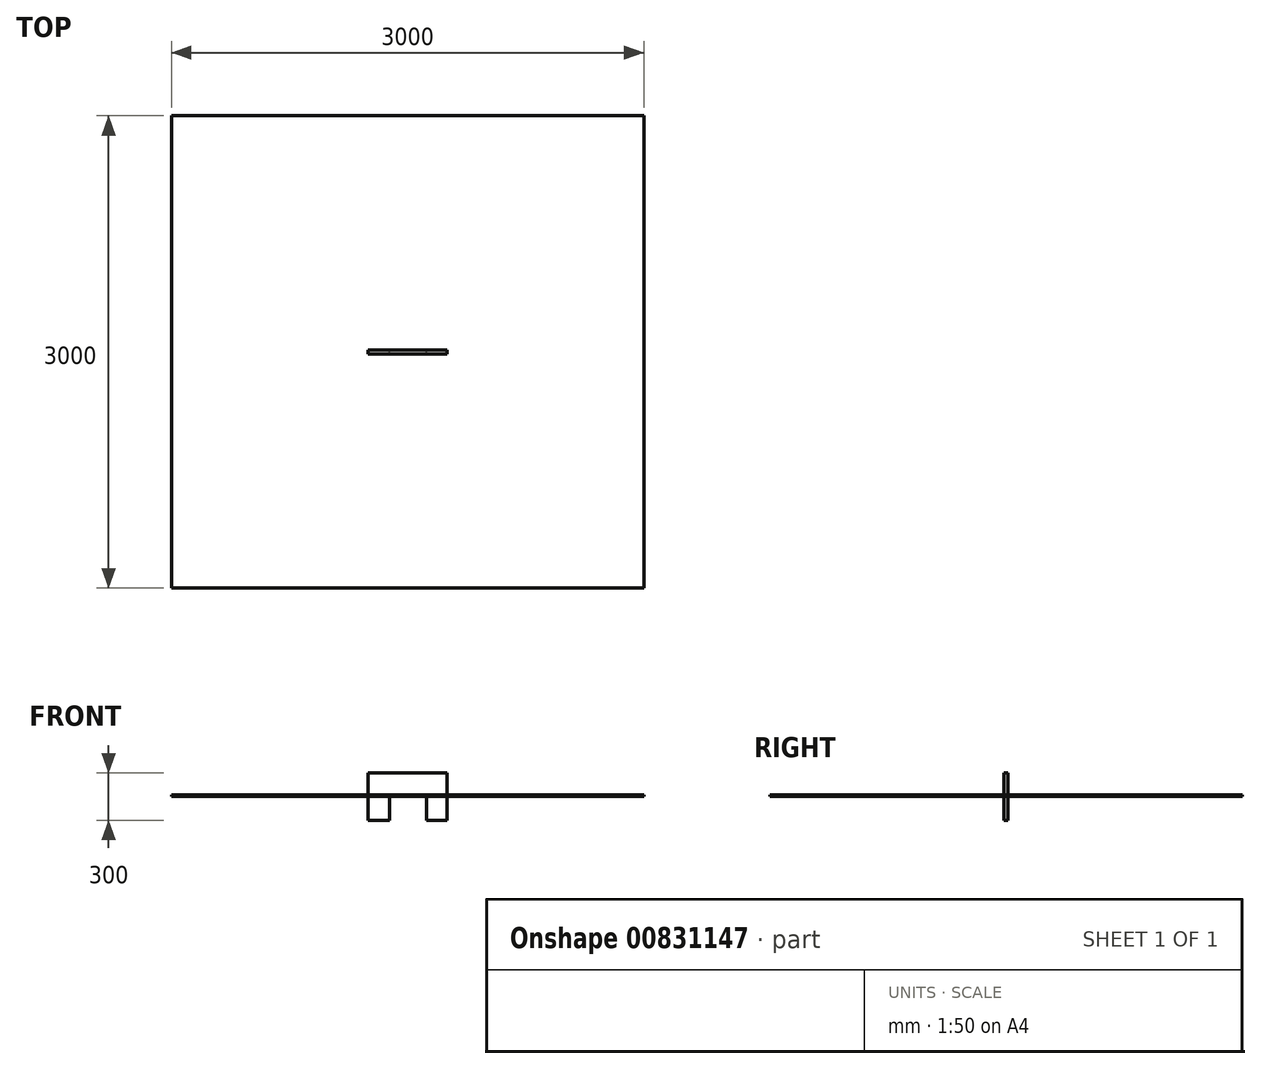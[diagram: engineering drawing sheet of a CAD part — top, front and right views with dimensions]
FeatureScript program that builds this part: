
annotation { "Feature Type Name" : "Feature", "Feature Type Description" : "" }
export const myFeature = defineFeature(function(context is Context, id is Id, definition is map)
    precondition{}
    {
        {
            var Q0;
            Q0=qCreatedBy(makeId("Top.planeOp"),FACE);
            var sketch = newSketch(context, id + "F0", { "sketchPlane" : qUnion([Q0])});
            skLineSegment(sketch, "E0.bottom", {"start": v(-1500, -1500) * mm, "end": v(1500, -1500) * mm});
            skLineSegment(sketch, "E0.top", {"start": v(-1500, 1500) * mm, "end": v(1500, 1500) * mm});
            skLineSegment(sketch, "E0.left", {"start": v(-1500, -1500) * mm, "end": v(-1500, 1500) * mm});
            skLineSegment(sketch, "E0.right", {"start": v(1500, -1500) * mm, "end": v(1500, 1500) * mm});
            skSolve(sketch);
        }
        {
            var Q0;
            Q0 = qSketchRegion(id + "F0", true);
            extrude(context, id + "F1", {"entities" : qUnion([Q0]), "depth" : 10 * mm, "offsetDistance" : 25 * mm});
        }
        {
            var Q0;
            Q0=qCreatedBy(makeId("Front.planeOp"),FACE);
            var sketch = newSketch(context, id + "F2", { "sketchPlane" : qUnion([Q0])});
            skLineSegment(sketch, "E1.bottom", {"start": v(-250, 150) * mm, "end": v(250, 150) * mm});
            skLineSegment(sketch, "E1.top", {"start": v(-250, -150) * mm, "end": v(-114.3, -150) * mm});
            skLineSegment(sketch, "E1.left", {"start": v(-250, 150) * mm, "end": v(-250, -150) * mm});
            skLineSegment(sketch, "E1.right", {"start": v(250, 150) * mm, "end": v(250, -150) * mm});
            skLineSegment(sketch, "E2.top", {"start": v(-114.3, 0) * mm, "end": v(119.98, 0) * mm});
            skLineSegment(sketch, "E2.left", {"start": v(-114.3, -150) * mm, "end": v(-114.3, 0) * mm});
            skLineSegment(sketch, "E2.right", {"start": v(119.98, -150) * mm, "end": v(119.98, 0) * mm});
            skLineSegment(sketch, "E3.trimOffspring", {"start": v(119.98, -150) * mm, "end": v(250, -150) * mm});
            skSolve(sketch);
        }
        {
            var Q0;
            Q0=makeQuery(id+"F2.imprint","IMPRINT",FACE,{"disambiguationData":[TD([[makeQuery(id+"F2.imprint","IMPRINT",EDGE,{"derivedFrom":sQuery(id+"F2.wireOp",EDGE,"E1.bottom")}),-1.0]])]});
            extrude(context, id + "F3", {"entities" : qUnion([Q0]), "endBound" : BoundingType.SYMMETRIC, "depth" : 25 * mm, "offsetDistance" : 25 * mm});
        }
    });
